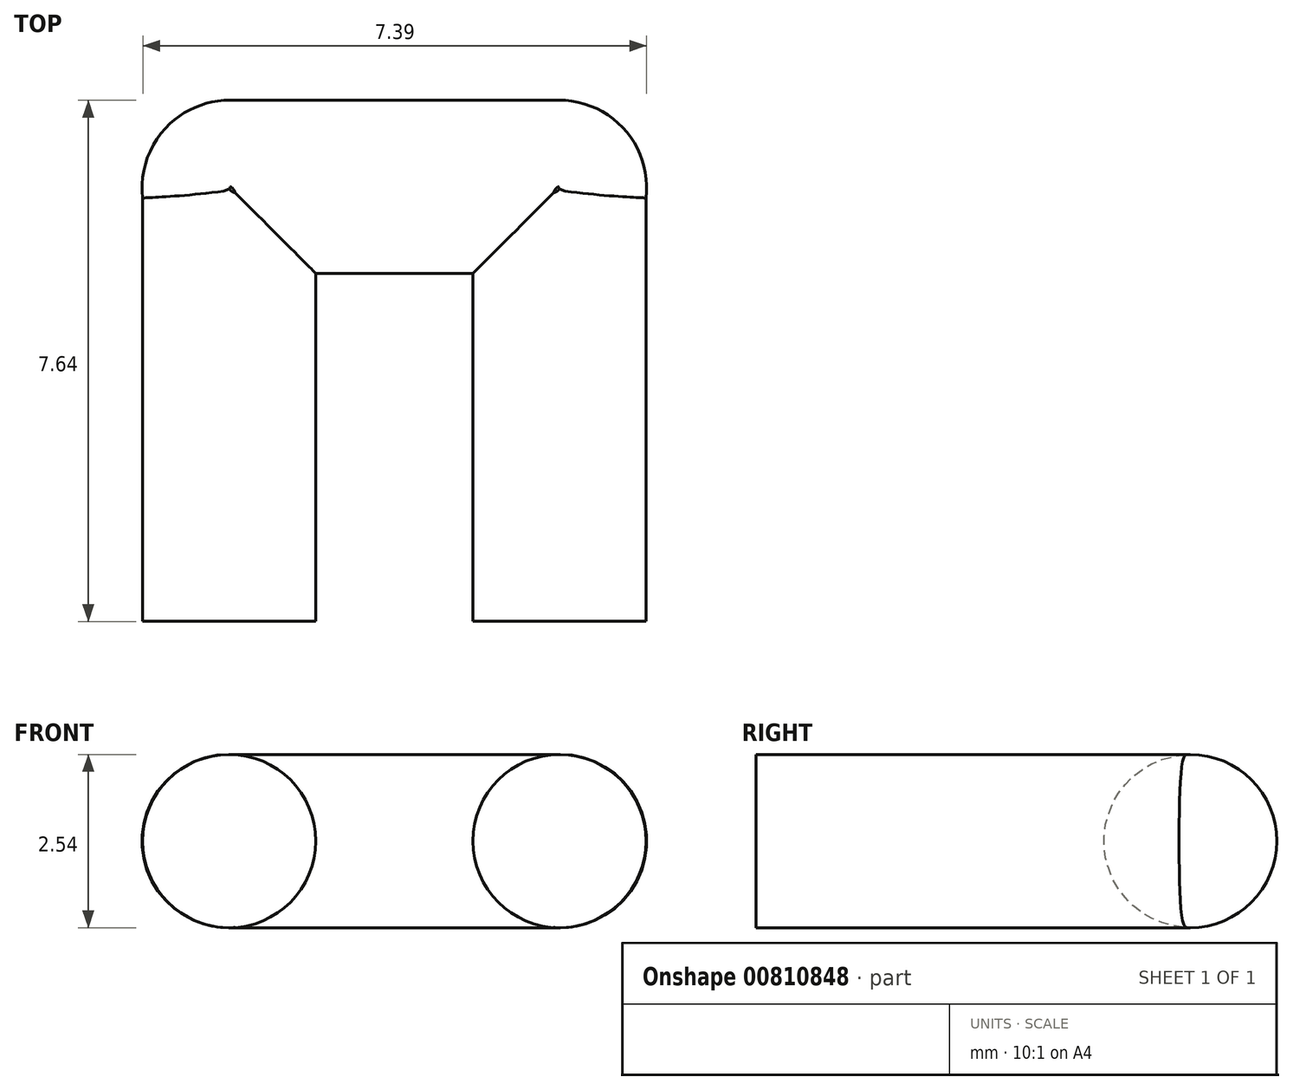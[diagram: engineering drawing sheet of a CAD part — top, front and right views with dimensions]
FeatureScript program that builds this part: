
annotation { "Feature Type Name" : "Feature", "Feature Type Description" : "" }
export const myFeature = defineFeature(function(context is Context, id is Id, definition is map)
    precondition{}
    {
        {
            var Q0;
            Q0=qCreatedBy(makeId("Front.planeOp"),FACE);
            var sketch = newSketch(context, id + "F0", { "sketchPlane" : qUnion([Q0])});
            skCircle(sketch, "E0", {"center": v(2.42, 0) * mm, "radius": 1.27 * mm});
            skCircle(sketch, "E1.MirrorC", {"center": v(-2.42, 0) * mm, "radius": 1.27 * mm});
            skSolve(sketch);
        }
        {
            var Q0;
            Q0 = qSketchRegion(id + "F0", true);
            extrude(context, id + "F1", {"entities" : qUnion([Q0]), "endBound" : BoundingType.SYMMETRIC, "depth" : 6.35 * mm, "offsetDistance" : 25.4 * mm});
        }
        {
            var Q0;
            Q0=qCreatedBy(makeId("Right.planeOp"),FACE);
            var sketch = newSketch(context, id + "F2", { "sketchPlane" : qUnion([Q0])});
            skCircle(sketch, "E2", {"center": v(3.2, 0) * mm, "radius": 1.27 * mm});
            skSolve(sketch);
        }
        {
            var Q0;
            Q0 = qSketchRegion(id + "F2", true);
            extrude(context, id + "F3", {"entities" : qUnion([Q0]), "operationType" : NewBodyOperationType.ADD, "endBound" : BoundingType.SYMMETRIC, "depth" : 4.83 * mm, "offsetDistance" : 25.4 * mm});
        }
        {
            var Q0;
            Q0=makeQuery(id+"F3.opExtrude","CAP_FACE",FACE,{"disambiguationData":[OSD([sQuery(id+"F2.wireOp",EDGE,"E2")])],"isStart":true});
            var sketch = newSketch(context, id + "F4", { "sketchPlane" : qUnion([Q0])});
            skSolve(sketch);
        }
        {
            var Q0;
            {var subQ0=sQuery(id+"F2.wireOp",EDGE,"E2");Q0=makeQuery(id+"F4.imprint","IMPRINT",FACE,{"disambiguationData":[TD([[makeQuery(id+"F4.imprint","IMPRINT",EDGE,{"derivedFrom":makeQuery(id+"F3.opExtrude","CAP_EDGE",EDGE,{"disambiguationData":[OSD([subQ0])],"isStart":true})}),-1.0]])]});}
            var Q1;
            Q1=makeQuery(id+"F3.boolean.opBoolean","INTERSECT",EDGE,{"derivedFrom":[makeQuery(id+"F1.opExtrude","CAP_FACE",FACE,{"disambiguationData":[OSD([sQuery(id+"F0.wireOp",EDGE,"E1.MirrorC")])],"isStart":true}),makeQuery(id+"F3.opExtrude","CAP_FACE",FACE,{"disambiguationData":[OSD([sQuery(id+"F2.wireOp",EDGE,"E2")])],"isStart":true})]});
            revolve(context, id + "F5", {"operationType" : NewBodyOperationType.ADD, "surfaceOperationType" : NewSurfaceOperationType.NEW, "entities" : qUnion([Q0]), "axis" : qUnion([Q1]), "revolveType" : RevolveType.FULL});
        }
        {
            var Q0;
            Q0=makeQuery(id+"F3.opExtrude","CAP_FACE",FACE,{"disambiguationData":[OSD([sQuery(id+"F2.wireOp",EDGE,"E2")])],"isStart":false});
            var sketch = newSketch(context, id + "F6", { "sketchPlane" : qUnion([Q0])});
            skSolve(sketch);
        }
        {
            var Q0;
            {var subQ0=sQuery(id+"F2.wireOp",EDGE,"E2");Q0=makeQuery(id+"F6.imprint","IMPRINT",FACE,{"disambiguationData":[TD([[makeQuery(id+"F6.imprint","IMPRINT",EDGE,{"derivedFrom":makeQuery(id+"F3.opExtrude","CAP_EDGE",EDGE,{"disambiguationData":[OSD([subQ0])],"isStart":false})}),1.0]])]});}
            var Q1;
            Q1=makeQuery(id+"F3.boolean.opBoolean","INTERSECT",EDGE,{"derivedFrom":[makeQuery(id+"F1.opExtrude","CAP_FACE",FACE,{"disambiguationData":[OSD([sQuery(id+"F0.wireOp",EDGE,"E0")])],"isStart":true}),makeQuery(id+"F3.opExtrude","CAP_FACE",FACE,{"disambiguationData":[OSD([sQuery(id+"F2.wireOp",EDGE,"E2")])],"isStart":false})]});
            revolve(context, id + "F7", {"operationType" : NewBodyOperationType.ADD, "surfaceOperationType" : NewSurfaceOperationType.NEW, "entities" : qUnion([Q0]), "axis" : qUnion([Q1]), "revolveType" : RevolveType.FULL});
        }
    });
